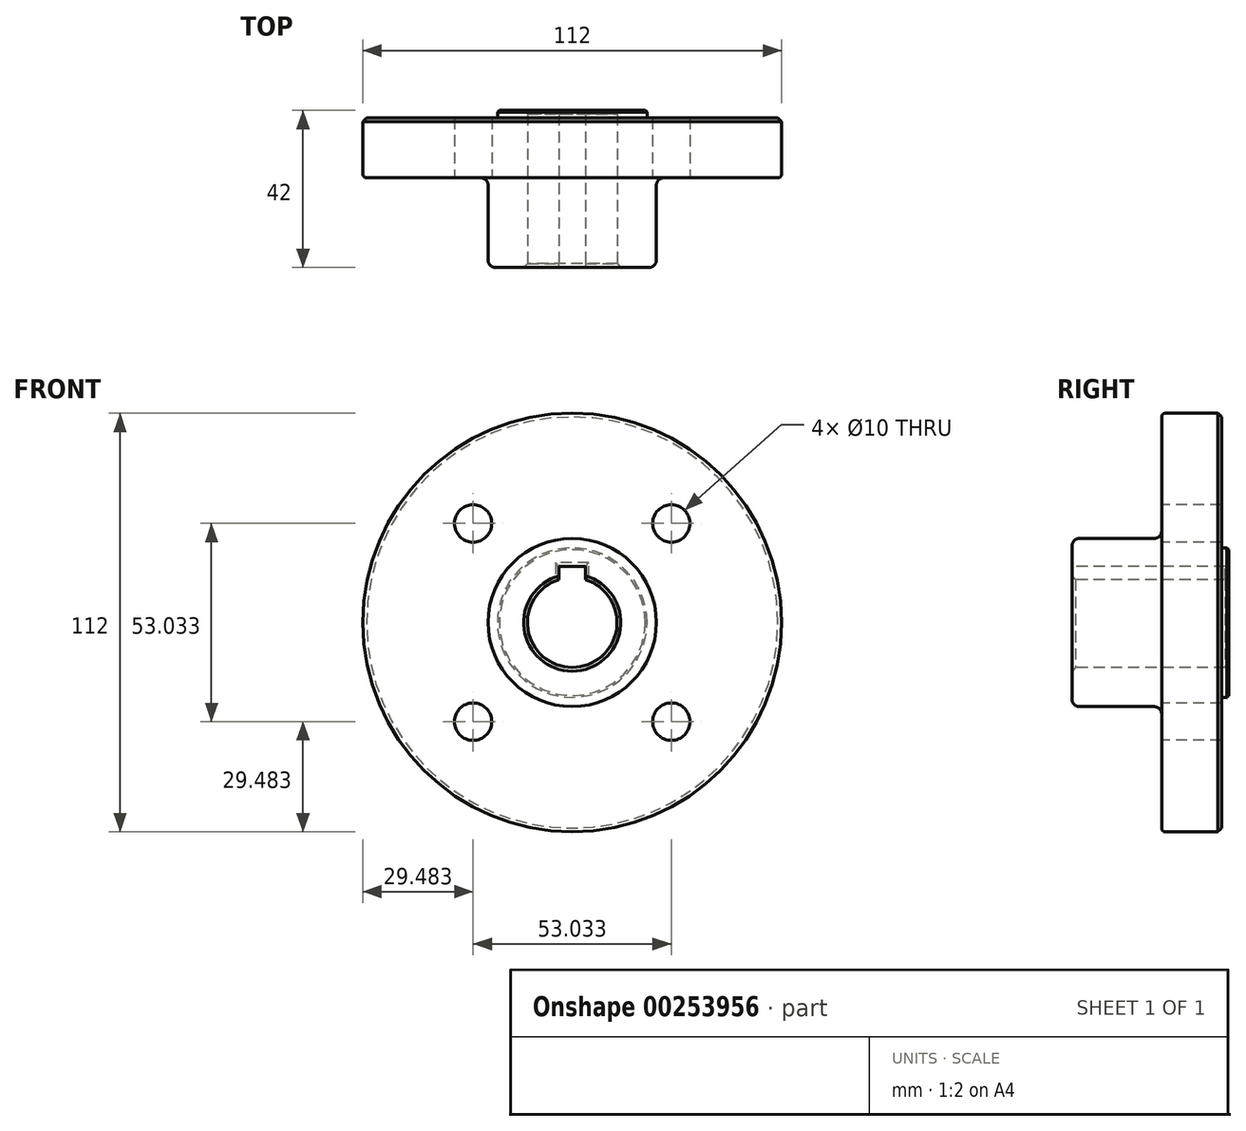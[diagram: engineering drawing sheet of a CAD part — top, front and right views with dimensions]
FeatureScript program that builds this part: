
annotation { "Feature Type Name" : "Feature", "Feature Type Description" : "" }
export const myFeature = defineFeature(function(context is Context, id is Id, definition is map)
    precondition{}
    {
        {
            var Q0;
            Q0=qCreatedBy(makeId("Right.planeOp"),FACE);
            var sketch = newSketch(context, id + "F0", { "sketchPlane" : qUnion([Q0])});
            skLineSegment(sketch, "E0", {"start": v(0, 20) * mm, "end": v(-2, 20) * mm});
            skLineSegment(sketch, "E1", {"start": v(-2, 20) * mm, "end": v(-2, 56) * mm});
            skLineSegment(sketch, "E2", {"start": v(-2, 56) * mm, "end": v(-18, 56) * mm});
            skLineSegment(sketch, "E3", {"start": v(-18, 56) * mm, "end": v(-18, 22.5) * mm});
            skLineSegment(sketch, "E4", {"start": v(-18, 22.5) * mm, "end": v(-42, 22.5) * mm});
            skLineSegment(sketch, "E5", {"start": v(-42, 22.5) * mm, "end": v(-42, 12) * mm});
            skLineSegment(sketch, "E6", {"start": v(-42, 12) * mm, "end": v(0, 12) * mm});
            skLineSegment(sketch, "E7", {"start": v(0, 12) * mm, "end": v(0, 20) * mm});
            skLineSegment(sketch, "E8", {"start": v(-41.93, 0) * mm, "end": v(6.58, 0) * mm, "construction": true});
            skSolve(sketch);
        }
        {
            var Q0;
            Q0=makeQuery(id+"F0.imprint","IMPRINT",FACE,{"disambiguationData":[TD([[makeQuery(id+"F0.imprint","IMPRINT",EDGE,{"derivedFrom":sQuery(id+"F0.wireOp",EDGE,"E0")}),1.0]])]});
            var Q1;
            Q1=sQuery(id+"F0.wireOp",EDGE,"E8");
            revolve(context, id + "F1", {"entities" : qUnion([Q0]), "axis" : qUnion([Q1]), "revolveType" : RevolveType.FULL});
        }
        {
            var Q0;
            Q0=makeQuery(id+"F1.opRevolve","SWEPT_FACE",FACE,{"disambiguationData":[OSD([sQuery(id+"F0.wireOp",EDGE,"E5")])]});
            var sketch = newSketch(context, id + "F2", { "sketchPlane" : qUnion([Q0])});
            skLineSegment(sketch, "E9.bottom", {"start": v(-3.5, 15) * mm, "end": v(3.5, 15) * mm});
            skLineSegment(sketch, "E9.top", {"start": v(-3.5, 8) * mm, "end": v(3.5, 8) * mm});
            skLineSegment(sketch, "E9.left", {"start": v(-3.5, 15) * mm, "end": v(-3.5, 8) * mm});
            skLineSegment(sketch, "E9.right", {"start": v(3.5, 15) * mm, "end": v(3.5, 8) * mm});
            skSolve(sketch);
        }
        {
            var Q0;
            Q0 = qSketchRegion(id + "F2", true);
            extrude(context, id + "F3", {"entities" : qUnion([Q0]), "operationType" : NewBodyOperationType.REMOVE, "endBound" : BoundingType.THROUGH_ALL, "oppositeDirection" : true, "depth" : 25 * mm});
        }
        {
            var Q0;
            Q0=makeQuery(id+"F1.opRevolve","SWEPT_FACE",FACE,{"disambiguationData":[OSD([sQuery(id+"F0.wireOp",EDGE,"E3")])]});
            var sketch = newSketch(context, id + "F4", { "sketchPlane" : qUnion([Q0])});
            skCircle(sketch, "E10", {"center": v(0, 0) * mm, "radius": 37.5 * mm, "construction": true});
            skLineSegment(sketch, "E11", {"start": v(0, 0) * mm, "end": v(32.94, 32.94) * mm, "construction": true});
            skPoint(sketch, "E12", {"position": v(26.52, 26.52) * mm});
            skPoint(sketch, "E13.1.0", {"position": v(-26.52, 26.52) * mm});
            skPoint(sketch, "E13.2.0", {"position": v(-26.52, -26.52) * mm});
            skPoint(sketch, "E13.3.0", {"position": v(26.52, -26.52) * mm});
            skSolve(sketch);
        }
        {
            var Q0;
            Q0=sQuery(id+"F4.wireOp",VERTEX,"E12");
            var Q1;
            Q1=sQuery(id+"F4.wireOp",VERTEX,"E13.3.0");
            var Q2;
            Q2=sQuery(id+"F4.wireOp",VERTEX,"E13.1.0");
            var Q3;
            Q3=sQuery(id+"F4.wireOp",VERTEX,"E13.2.0");
            var Q4;
            Q4=makeQuery(id+"F1.opRevolve","SWEPT_BODY",BODY,{"disambiguationData":[OSD([sQuery(id+"F0.wireOp",EDGE,"E0"),sQuery(id+"F0.wireOp",EDGE,"E1"),sQuery(id+"F0.wireOp",EDGE,"E2"),sQuery(id+"F0.wireOp",EDGE,"E3"),sQuery(id+"F0.wireOp",EDGE,"E4"),sQuery(id+"F0.wireOp",EDGE,"E5"),sQuery(id+"F0.wireOp",EDGE,"E6"),sQuery(id+"F0.wireOp",EDGE,"E7")])]});
            hole(context, id + "F5", {"style" : HoleStyle.SIMPLE, "endStyle" : HoleEndStyle.THROUGH, "holeDiameter" : 10 * mm, "tappedDepth" : 12 * mm, "tapClearance" : 3, "locations" : qUnion([Q0, Q1, Q2, Q3]), "scope" : qUnion([Q4])});
        }
        {
            var Q0;
            Q0=makeQuery(id+"F3.boolean.opBoolean","COPY",EDGE,{"derivedFrom":makeQuery(id+"F3.opExtrude","CAP_EDGE",EDGE,{"disambiguationData":[OSD([sQuery(id+"F2.wireOp",EDGE,"E9.right")])],"isStart":true})});
            var Q1;
            Q1=makeQuery(id+"F3.boolean.opBoolean","INTERSECT",EDGE,{"derivedFrom":[makeQuery(id+"F1.opRevolve","SWEPT_FACE",FACE,{"disambiguationData":[OSD([sQuery(id+"F0.wireOp",EDGE,"E7")])]}),makeQuery(id+"F3.opExtrude","SWEPT_FACE",FACE,{"disambiguationData":[OSD([sQuery(id+"F2.wireOp",EDGE,"E9.right")])]})]});
            var Q2;
            Q2=makeQuery(id+"F3.boolean.opBoolean","INTERSECT",EDGE,{"derivedFrom":[makeQuery(id+"F1.opRevolve","SWEPT_FACE",FACE,{"disambiguationData":[OSD([sQuery(id+"F0.wireOp",EDGE,"E7")])]}),makeQuery(id+"F3.opExtrude","SWEPT_FACE",FACE,{"disambiguationData":[OSD([sQuery(id+"F2.wireOp",EDGE,"E9.left")])]})]});
            var Q3;
            Q3=makeQuery(id+"F3.boolean.opBoolean","INTERSECT",EDGE,{"derivedFrom":[makeQuery(id+"F1.opRevolve","SWEPT_FACE",FACE,{"disambiguationData":[OSD([sQuery(id+"F0.wireOp",EDGE,"E7")])]}),makeQuery(id+"F3.opExtrude","SWEPT_FACE",FACE,{"disambiguationData":[OSD([sQuery(id+"F2.wireOp",EDGE,"E9.bottom")])]})]});
            var Q4;
            Q4=makeQuery(id+"F1.opRevolve","SWEPT_EDGE",EDGE,{"disambiguationData":[OSD([sQuery(id+"F0.wireOp",EDGE,"E6"),sQuery(id+"F0.wireOp",EDGE,"E7")])]});
            var Q5;
            Q5=makeQuery(id+"F1.opRevolve","SWEPT_EDGE",EDGE,{"disambiguationData":[OSD([sQuery(id+"F0.wireOp",EDGE,"E5"),sQuery(id+"F0.wireOp",EDGE,"E6")])]});
            var Q6;
            Q6=makeQuery(id+"F3.boolean.opBoolean","COPY",EDGE,{"derivedFrom":makeQuery(id+"F3.opExtrude","CAP_EDGE",EDGE,{"disambiguationData":[OSD([sQuery(id+"F2.wireOp",EDGE,"E9.left")])],"isStart":true})});
            var Q7;
            Q7=makeQuery(id+"F3.boolean.opBoolean","COPY",EDGE,{"derivedFrom":makeQuery(id+"F3.opExtrude","CAP_EDGE",EDGE,{"disambiguationData":[OSD([sQuery(id+"F2.wireOp",EDGE,"E9.bottom")])],"isStart":true})});
            chamfer(context, id + "F6", {"entities" : qUnion([Q0, Q1, Q2, Q3, Q4, Q5, Q6, Q7]), "width" : 1 * mm, "tangentPropagation" : true});
        }
        {
            var Q0;
            Q0=makeQuery(id+"F1.opRevolve","SWEPT_EDGE",EDGE,{"disambiguationData":[OSD([sQuery(id+"F0.wireOp",EDGE,"E0"),sQuery(id+"F0.wireOp",EDGE,"E7")])]});
            chamfer(context, id + "F7", {"entities" : qUnion([Q0]), "width" : 0.5 * mm, "tangentPropagation" : true});
        }
        {
            var Q0;
            Q0=makeQuery(id+"F1.opRevolve","SWEPT_EDGE",EDGE,{"disambiguationData":[OSD([sQuery(id+"F0.wireOp",EDGE,"E1"),sQuery(id+"F0.wireOp",EDGE,"E2")])]});
            chamfer(context, id + "F8", {"entities" : qUnion([Q0]), "width" : 1 * mm, "tangentPropagation" : true});
        }
        {
            var Q0;
            Q0=makeQuery(id+"F1.opRevolve","SWEPT_EDGE",EDGE,{"disambiguationData":[OSD([sQuery(id+"F0.wireOp",EDGE,"E2"),sQuery(id+"F0.wireOp",EDGE,"E3")])]});
            fillet(context, id + "F9", {"entities" : qUnion([Q0]), "radius" : 1 * mm, "tangentPropagation" : true, "allowEdgeOverflow" : false});
        }
        {
            var Q0;
            Q0=makeQuery(id+"F1.opRevolve","SWEPT_EDGE",EDGE,{"disambiguationData":[OSD([sQuery(id+"F0.wireOp",EDGE,"E3"),sQuery(id+"F0.wireOp",EDGE,"E4")])]});
            var Q1;
            Q1=makeQuery(id+"F1.opRevolve","SWEPT_EDGE",EDGE,{"disambiguationData":[OSD([sQuery(id+"F0.wireOp",EDGE,"E4"),sQuery(id+"F0.wireOp",EDGE,"E5")])]});
            fillet(context, id + "F10", {"entities" : qUnion([Q0, Q1]), "radius" : 2 * mm, "tangentPropagation" : true, "allowEdgeOverflow" : false});
        }
        {
            var Q0;
            Q0=makeQuery(id+"F1.opRevolve","SWEPT_EDGE",EDGE,{"disambiguationData":[OSD([sQuery(id+"F0.wireOp",EDGE,"E0"),sQuery(id+"F0.wireOp",EDGE,"E1")])]});
            fillet(context, id + "F11", {"entities" : qUnion([Q0]), "radius" : 0.5 * mm, "tangentPropagation" : true, "allowEdgeOverflow" : false});
        }
    });
